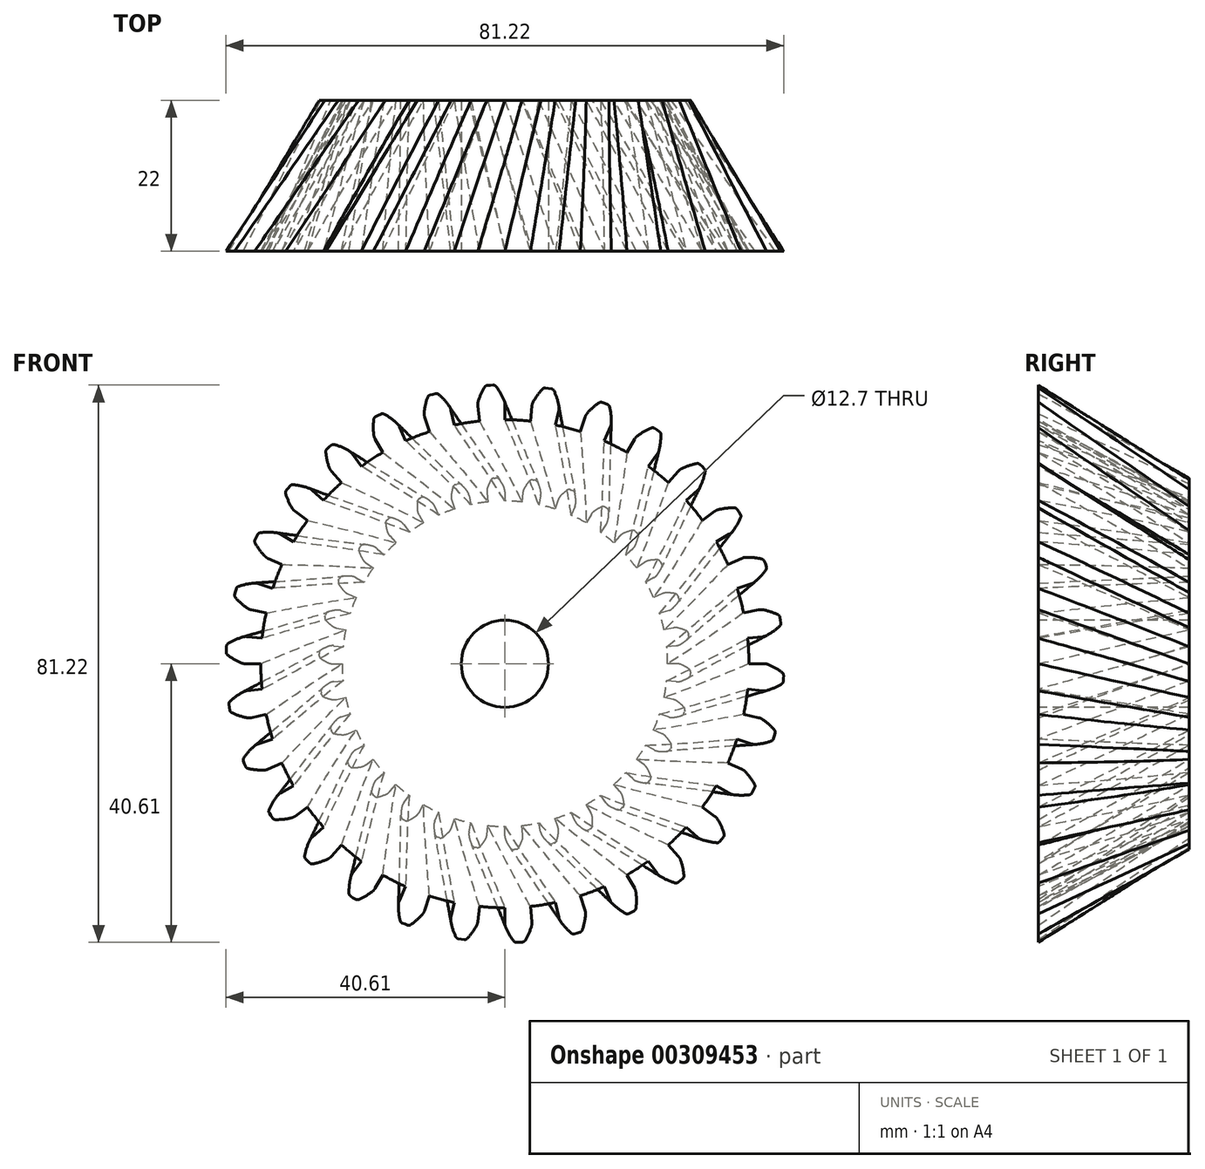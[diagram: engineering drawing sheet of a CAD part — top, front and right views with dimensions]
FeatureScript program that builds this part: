
annotation { "Feature Type Name" : "Feature", "Feature Type Description" : "" }
export const myFeature = defineFeature(function(context is Context, id is Id, definition is map)
    precondition{}
    {
        {
            var Q0;
            Q0=qCreatedBy(makeId("Front.planeOp"),FACE);
            var sketch = newSketch(context, id + "F0", { "sketchPlane" : qUnion([Q0])});
            skCircle(sketch, "E0", {"center": v(0, 0) * mm, "radius": 23.71 * mm});
            skArc(sketch, "E1.trimOffspring", {"start": v(-0.14, 25.74) * mm, "mid": v(-0.44, 26.31) * mm, "end": v(-0.8, 26.85) * mm});
            skLineSegment(sketch, "E2", {"start": v(0, 25.08) * mm, "end": v(0, 23.71) * mm});
            skLineSegment(sketch, "E3", {"start": v(-1.22, 27.06) * mm, "end": v(-1.42, 27.06) * mm});
            skLineSegment(sketch, "E4.MirrorCS", {"start": v(-1.62, 27.04) * mm, "end": v(-1.42, 27.06) * mm});
            skArc(sketch, "E5.MirrorCS", {"start": v(-2.55, 25.61) * mm, "mid": v(-2.31, 26.22) * mm, "end": v(-2.02, 26.79) * mm});
            skLineSegment(sketch, "E6.MirrorCS", {"start": v(-2.62, 24.94) * mm, "end": v(-2.48, 23.58) * mm});
            skPoint(sketch, "E7.visualSharp", {"position": v(-2.66, 25.26) * mm});
            skArc(sketch, "E7.filletArc", {"start": v(-2.55, 25.61) * mm, "mid": v(-2.62, 25.28) * mm, "end": v(-2.62, 24.94) * mm});
            skPoint(sketch, "E8.visualSharp", {"position": v(0, 25.4) * mm});
            skArc(sketch, "E8.filletArc", {"start": v(0, 25.08) * mm, "mid": v(-0.04, 25.42) * mm, "end": v(-0.14, 25.74) * mm});
            skPoint(sketch, "E9.visualSharp", {"position": v(-1.88, 27.02) * mm});
            skArc(sketch, "E9.filletArc", {"start": v(-1.62, 27.04) * mm, "mid": v(-1.85, 26.97) * mm, "end": v(-2.02, 26.79) * mm});
            skPoint(sketch, "E10.visualSharp", {"position": v(-0.96, 27.07) * mm});
            skArc(sketch, "E10.filletArc", {"start": v(-0.8, 26.85) * mm, "mid": v(-0.98, 27.01) * mm, "end": v(-1.22, 27.06) * mm});
            skSolve(sketch);
        }
        {
            var Q0;
            Q0=qCreatedBy(makeId("Front.planeOp"),FACE);
            cPlane(context, id + "F1", {"entities" : qUnion([Q0]), "cplaneType" : CPlaneType.OFFSET, "offset" : 22 * mm, "width" : 152.4 * mm, "height" : 152.4 * mm});
        }
        {
            var Q0;
            Q0=qCreatedBy(id+"F1.planeOp",FACE);
            var sketch = newSketch(context, id + "F2", { "sketchPlane" : qUnion([Q0])});
            skCircle(sketch, "E11", {"center": v(0, 0) * mm, "radius": 35.56 * mm});
            skArc(sketch, "E12.trimOffspring", {"start": v(-0.13, 38.42) * mm, "mid": v(-0.64, 39.44) * mm, "end": v(-1.28, 40.4) * mm});
            skLineSegment(sketch, "E13", {"start": v(0, 37.79) * mm, "end": v(0, 35.56) * mm});
            skLineSegment(sketch, "E14", {"start": v(-1.7, 40.6) * mm, "end": v(-2.13, 40.6) * mm});
            skLineSegment(sketch, "E15.MirrorCS", {"start": v(-2.55, 40.56) * mm, "end": v(-2.13, 40.6) * mm});
            skArc(sketch, "E16.MirrorCS", {"start": v(-3.89, 38.22) * mm, "mid": v(-3.48, 39.3) * mm, "end": v(-2.95, 40.31) * mm});
            skLineSegment(sketch, "E17.MirrorCS", {"start": v(-3.95, 37.58) * mm, "end": v(-3.72, 35.37) * mm});
            skPoint(sketch, "E18.visualSharp", {"position": v(-3.98, 37.9) * mm});
            skArc(sketch, "E18.filletArc", {"start": v(-3.89, 38.22) * mm, "mid": v(-3.95, 37.9) * mm, "end": v(-3.95, 37.58) * mm});
            skPoint(sketch, "E19.visualSharp", {"position": v(0, 38.1) * mm});
            skArc(sketch, "E19.filletArc", {"start": v(0, 37.79) * mm, "mid": v(-0.03, 38.1) * mm, "end": v(-0.13, 38.42) * mm});
            skPoint(sketch, "E20.visualSharp", {"position": v(-2.81, 40.54) * mm});
            skArc(sketch, "E20.filletArc", {"start": v(-2.55, 40.56) * mm, "mid": v(-2.78, 40.49) * mm, "end": v(-2.95, 40.31) * mm});
            skPoint(sketch, "E21.visualSharp", {"position": v(-1.44, 40.61) * mm});
            skArc(sketch, "E21.filletArc", {"start": v(-1.28, 40.4) * mm, "mid": v(-1.46, 40.56) * mm, "end": v(-1.7, 40.6) * mm});
            skLineSegment(sketch, "E22.1.0", {"start": v(-10.93, 39.14) * mm, "end": v(-10.52, 39.26) * mm});
            skLineSegment(sketch, "E22.1.1", {"start": v(-10.1, 39.36) * mm, "end": v(-10.52, 39.26) * mm});
            skArc(sketch, "E22.1.2", {"start": v(-9.65, 39.25) * mm, "mid": v(-9.86, 39.37) * mm, "end": v(-10.1, 39.36) * mm});
            skArc(sketch, "E22.1.3", {"start": v(-10.93, 39.14) * mm, "mid": v(-11.14, 39.02) * mm, "end": v(-11.27, 38.82) * mm});
            skArc(sketch, "E22.1.4", {"start": v(-11.75, 36.58) * mm, "mid": v(-11.58, 37.71) * mm, "end": v(-11.27, 38.82) * mm});
            skArc(sketch, "E22.1.5", {"start": v(-8.11, 37.55) * mm, "mid": v(-8.83, 38.45) * mm, "end": v(-9.65, 39.25) * mm});
            skArc(sketch, "E22.1.6", {"start": v(-7.86, 36.96) * mm, "mid": v(-7.95, 37.27) * mm, "end": v(-8.11, 37.55) * mm});
            skArc(sketch, "E22.1.7", {"start": v(-11.75, 36.58) * mm, "mid": v(-11.75, 36.25) * mm, "end": v(-11.68, 35.94) * mm});
            skLineSegment(sketch, "E22.1.8", {"start": v(-11.68, 35.94) * mm, "end": v(-10.99, 33.82) * mm});
            skLineSegment(sketch, "E22.1.9", {"start": v(-7.86, 36.96) * mm, "end": v(-7.4, 34.78) * mm});
            skLineSegment(sketch, "E22.2.0", {"start": v(-18.83, 36.01) * mm, "end": v(-18.45, 36.22) * mm});
            skLineSegment(sketch, "E22.2.1", {"start": v(-18.07, 36.4) * mm, "end": v(-18.45, 36.22) * mm});
            skArc(sketch, "E22.2.2", {"start": v(-17.6, 36.4) * mm, "mid": v(-17.83, 36.45) * mm, "end": v(-18.07, 36.4) * mm});
            skArc(sketch, "E22.2.3", {"start": v(-18.83, 36.01) * mm, "mid": v(-19.01, 35.85) * mm, "end": v(-19.1, 35.63) * mm});
            skArc(sketch, "E22.2.4", {"start": v(-19.1, 33.33) * mm, "mid": v(-19.17, 34.48) * mm, "end": v(-19.1, 35.63) * mm});
            skArc(sketch, "E22.2.5", {"start": v(-15.74, 35.04) * mm, "mid": v(-16.63, 35.77) * mm, "end": v(-17.6, 36.4) * mm});
            skArc(sketch, "E22.2.6", {"start": v(-15.37, 34.52) * mm, "mid": v(-15.53, 34.8) * mm, "end": v(-15.74, 35.04) * mm});
            skArc(sketch, "E22.2.7", {"start": v(-19.1, 33.33) * mm, "mid": v(-19.03, 33.02) * mm, "end": v(-18.9, 32.73) * mm});
            skLineSegment(sketch, "E22.2.8", {"start": v(-18.9, 32.73) * mm, "end": v(-17.78, 30.8) * mm});
            skLineSegment(sketch, "E22.2.9", {"start": v(-15.37, 34.52) * mm, "end": v(-14.46, 32.49) * mm});
            skLineSegment(sketch, "E22.3.0", {"start": v(-25.9, 31.31) * mm, "end": v(-25.58, 31.59) * mm});
            skLineSegment(sketch, "E22.3.1", {"start": v(-25.24, 31.85) * mm, "end": v(-25.58, 31.59) * mm});
            skArc(sketch, "E22.3.2", {"start": v(-24.78, 31.94) * mm, "mid": v(-25.02, 31.95) * mm, "end": v(-25.24, 31.85) * mm});
            skArc(sketch, "E22.3.3", {"start": v(-25.9, 31.31) * mm, "mid": v(-26.05, 31.12) * mm, "end": v(-26.09, 30.88) * mm});
            skArc(sketch, "E22.3.4", {"start": v(-25.61, 28.63) * mm, "mid": v(-25.92, 29.74) * mm, "end": v(-26.09, 30.88) * mm});
            skArc(sketch, "E22.3.5", {"start": v(-22.68, 31) * mm, "mid": v(-23.7, 31.53) * mm, "end": v(-24.78, 31.94) * mm});
            skArc(sketch, "E22.3.6", {"start": v(-22.21, 30.57) * mm, "mid": v(-22.43, 30.81) * mm, "end": v(-22.68, 31) * mm});
            skArc(sketch, "E22.3.7", {"start": v(-25.61, 28.63) * mm, "mid": v(-25.48, 28.34) * mm, "end": v(-25.29, 28.08) * mm});
            skLineSegment(sketch, "E22.3.8", {"start": v(-25.29, 28.08) * mm, "end": v(-23.8, 26.43) * mm});
            skLineSegment(sketch, "E22.3.9", {"start": v(-22.21, 30.57) * mm, "end": v(-20.9, 28.77) * mm});
            skLineSegment(sketch, "E22.4.0", {"start": v(-31.85, 25.24) * mm, "end": v(-31.59, 25.58) * mm});
            skLineSegment(sketch, "E22.4.1", {"start": v(-31.31, 25.9) * mm, "end": v(-31.59, 25.58) * mm});
            skArc(sketch, "E22.4.2", {"start": v(-30.88, 26.09) * mm, "mid": v(-31.12, 26.05) * mm, "end": v(-31.31, 25.9) * mm});
            skArc(sketch, "E22.4.3", {"start": v(-31.85, 25.24) * mm, "mid": v(-31.95, 25.02) * mm, "end": v(-31.94, 24.78) * mm});
            skArc(sketch, "E22.4.4", {"start": v(-31, 22.68) * mm, "mid": v(-31.53, 23.7) * mm, "end": v(-31.94, 24.78) * mm});
            skArc(sketch, "E22.4.5", {"start": v(-28.63, 25.61) * mm, "mid": v(-29.74, 25.92) * mm, "end": v(-30.88, 26.09) * mm});
            skArc(sketch, "E22.4.6", {"start": v(-28.08, 25.29) * mm, "mid": v(-28.34, 25.48) * mm, "end": v(-28.63, 25.61) * mm});
            skArc(sketch, "E22.4.7", {"start": v(-31, 22.68) * mm, "mid": v(-30.81, 22.43) * mm, "end": v(-30.57, 22.21) * mm});
            skLineSegment(sketch, "E22.4.8", {"start": v(-30.57, 22.21) * mm, "end": v(-28.77, 20.9) * mm});
            skLineSegment(sketch, "E22.4.9", {"start": v(-28.08, 25.29) * mm, "end": v(-26.43, 23.8) * mm});
            skLineSegment(sketch, "E22.5.0", {"start": v(-36.4, 18.07) * mm, "end": v(-36.22, 18.45) * mm});
            skLineSegment(sketch, "E22.5.1", {"start": v(-36.01, 18.83) * mm, "end": v(-36.22, 18.45) * mm});
            skArc(sketch, "E22.5.2", {"start": v(-35.63, 19.1) * mm, "mid": v(-35.85, 19.01) * mm, "end": v(-36.01, 18.83) * mm});
            skArc(sketch, "E22.5.3", {"start": v(-36.4, 18.07) * mm, "mid": v(-36.45, 17.83) * mm, "end": v(-36.4, 17.6) * mm});
            skArc(sketch, "E22.5.4", {"start": v(-35.04, 15.74) * mm, "mid": v(-35.77, 16.63) * mm, "end": v(-36.4, 17.6) * mm});
            skArc(sketch, "E22.5.5", {"start": v(-33.33, 19.1) * mm, "mid": v(-34.48, 19.17) * mm, "end": v(-35.63, 19.1) * mm});
            skArc(sketch, "E22.5.6", {"start": v(-32.73, 18.9) * mm, "mid": v(-33.02, 19.03) * mm, "end": v(-33.33, 19.1) * mm});
            skArc(sketch, "E22.5.7", {"start": v(-35.04, 15.74) * mm, "mid": v(-34.8, 15.53) * mm, "end": v(-34.52, 15.37) * mm});
            skLineSegment(sketch, "E22.5.8", {"start": v(-34.52, 15.37) * mm, "end": v(-32.49, 14.46) * mm});
            skLineSegment(sketch, "E22.5.9", {"start": v(-32.73, 18.9) * mm, "end": v(-30.8, 17.78) * mm});
            skLineSegment(sketch, "E22.6.0", {"start": v(-39.36, 10.1) * mm, "end": v(-39.26, 10.52) * mm});
            skLineSegment(sketch, "E22.6.1", {"start": v(-39.14, 10.93) * mm, "end": v(-39.26, 10.52) * mm});
            skArc(sketch, "E22.6.2", {"start": v(-38.82, 11.27) * mm, "mid": v(-39.02, 11.14) * mm, "end": v(-39.14, 10.93) * mm});
            skArc(sketch, "E22.6.3", {"start": v(-39.36, 10.1) * mm, "mid": v(-39.37, 9.86) * mm, "end": v(-39.25, 9.65) * mm});
            skArc(sketch, "E22.6.4", {"start": v(-37.55, 8.11) * mm, "mid": v(-38.45, 8.83) * mm, "end": v(-39.25, 9.65) * mm});
            skArc(sketch, "E22.6.5", {"start": v(-36.58, 11.75) * mm, "mid": v(-37.71, 11.58) * mm, "end": v(-38.82, 11.27) * mm});
            skArc(sketch, "E22.6.6", {"start": v(-35.94, 11.68) * mm, "mid": v(-36.25, 11.75) * mm, "end": v(-36.58, 11.75) * mm});
            skArc(sketch, "E22.6.7", {"start": v(-37.55, 8.11) * mm, "mid": v(-37.27, 7.95) * mm, "end": v(-36.96, 7.86) * mm});
            skLineSegment(sketch, "E22.6.8", {"start": v(-36.96, 7.86) * mm, "end": v(-34.78, 7.4) * mm});
            skLineSegment(sketch, "E22.6.9", {"start": v(-35.94, 11.68) * mm, "end": v(-33.82, 10.99) * mm});
            skLineSegment(sketch, "E22.7.0", {"start": v(-40.6, 1.7) * mm, "end": v(-40.6, 2.13) * mm});
            skLineSegment(sketch, "E22.7.1", {"start": v(-40.56, 2.55) * mm, "end": v(-40.6, 2.13) * mm});
            skArc(sketch, "E22.7.2", {"start": v(-40.31, 2.95) * mm, "mid": v(-40.49, 2.78) * mm, "end": v(-40.56, 2.55) * mm});
            skArc(sketch, "E22.7.3", {"start": v(-40.6, 1.7) * mm, "mid": v(-40.56, 1.46) * mm, "end": v(-40.4, 1.28) * mm});
            skArc(sketch, "E22.7.4", {"start": v(-38.42, 0.13) * mm, "mid": v(-39.44, 0.64) * mm, "end": v(-40.4, 1.28) * mm});
            skArc(sketch, "E22.7.5", {"start": v(-38.22, 3.89) * mm, "mid": v(-39.3, 3.48) * mm, "end": v(-40.31, 2.95) * mm});
            skArc(sketch, "E22.7.6", {"start": v(-37.58, 3.95) * mm, "mid": v(-37.9, 3.95) * mm, "end": v(-38.22, 3.89) * mm});
            skArc(sketch, "E22.7.7", {"start": v(-38.42, 0.13) * mm, "mid": v(-38.1, 0.03) * mm, "end": v(-37.79, 0) * mm});
            skLineSegment(sketch, "E22.7.8", {"start": v(-37.79, 0) * mm, "end": v(-35.56, 0) * mm});
            skLineSegment(sketch, "E22.7.9", {"start": v(-37.58, 3.95) * mm, "end": v(-35.37, 3.72) * mm});
            skLineSegment(sketch, "E22.8.0", {"start": v(-40.07, -6.78) * mm, "end": v(-40.15, -6.36) * mm});
            skLineSegment(sketch, "E22.8.1", {"start": v(-40.2, -5.93) * mm, "end": v(-40.15, -6.36) * mm});
            skArc(sketch, "E22.8.2", {"start": v(-40.05, -5.5) * mm, "mid": v(-40.18, -5.7) * mm, "end": v(-40.2, -5.93) * mm});
            skArc(sketch, "E22.8.3", {"start": v(-40.07, -6.78) * mm, "mid": v(-39.97, -7) * mm, "end": v(-39.79, -7.15) * mm});
            skArc(sketch, "E22.8.4", {"start": v(-37.6, -7.86) * mm, "mid": v(-38.72, -7.57) * mm, "end": v(-39.79, -7.15) * mm});
            skArc(sketch, "E22.8.5", {"start": v(-38.2, -4.14) * mm, "mid": v(-39.16, -4.76) * mm, "end": v(-40.05, -5.5) * mm});
            skArc(sketch, "E22.8.6", {"start": v(-37.58, -3.95) * mm, "mid": v(-37.9, -4.02) * mm, "end": v(-38.2, -4.14) * mm});
            skArc(sketch, "E22.8.7", {"start": v(-37.6, -7.86) * mm, "mid": v(-37.28, -7.9) * mm, "end": v(-36.96, -7.86) * mm});
            skLineSegment(sketch, "E22.8.8", {"start": v(-36.96, -7.86) * mm, "end": v(-34.78, -7.4) * mm});
            skLineSegment(sketch, "E22.8.9", {"start": v(-37.58, -3.95) * mm, "end": v(-35.37, -3.72) * mm});
            skLineSegment(sketch, "E22.9.0", {"start": v(-37.79, -14.96) * mm, "end": v(-37.95, -14.57) * mm});
            skLineSegment(sketch, "E22.9.1", {"start": v(-38.1, -14.16) * mm, "end": v(-37.95, -14.57) * mm});
            skArc(sketch, "E22.9.2", {"start": v(-38.03, -13.7) * mm, "mid": v(-38.12, -13.92) * mm, "end": v(-38.1, -14.16) * mm});
            skArc(sketch, "E22.9.3", {"start": v(-37.79, -14.96) * mm, "mid": v(-37.64, -15.16) * mm, "end": v(-37.43, -15.27) * mm});
            skArc(sketch, "E22.9.4", {"start": v(-35.15, -15.5) * mm, "mid": v(-36.3, -15.46) * mm, "end": v(-37.43, -15.27) * mm});
            skArc(sketch, "E22.9.5", {"start": v(-36.5, -12) * mm, "mid": v(-37.32, -12.8) * mm, "end": v(-38.03, -13.7) * mm});
            skArc(sketch, "E22.9.6", {"start": v(-35.94, -11.68) * mm, "mid": v(-36.23, -11.8) * mm, "end": v(-36.5, -12) * mm});
            skArc(sketch, "E22.9.7", {"start": v(-35.15, -15.5) * mm, "mid": v(-34.83, -15.47) * mm, "end": v(-34.52, -15.37) * mm});
            skLineSegment(sketch, "E22.9.8", {"start": v(-34.52, -15.37) * mm, "end": v(-32.49, -14.46) * mm});
            skLineSegment(sketch, "E22.9.9", {"start": v(-35.94, -11.68) * mm, "end": v(-33.82, -10.99) * mm});
            skLineSegment(sketch, "E22.10.0", {"start": v(-33.85, -22.5) * mm, "end": v(-34.09, -22.14) * mm});
            skLineSegment(sketch, "E22.10.1", {"start": v(-34.32, -21.77) * mm, "end": v(-34.09, -22.14) * mm});
            skArc(sketch, "E22.10.2", {"start": v(-34.35, -21.3) * mm, "mid": v(-34.4, -21.54) * mm, "end": v(-34.32, -21.77) * mm});
            skArc(sketch, "E22.10.3", {"start": v(-33.85, -22.5) * mm, "mid": v(-33.67, -22.66) * mm, "end": v(-33.44, -22.72) * mm});
            skArc(sketch, "E22.10.4", {"start": v(-31.15, -22.48) * mm, "mid": v(-32.29, -22.67) * mm, "end": v(-33.44, -22.72) * mm});
            skArc(sketch, "E22.10.5", {"start": v(-33.2, -19.32) * mm, "mid": v(-33.84, -20.28) * mm, "end": v(-34.35, -21.3) * mm});
            skArc(sketch, "E22.10.6", {"start": v(-32.73, -18.9) * mm, "mid": v(-32.99, -19.08) * mm, "end": v(-33.2, -19.32) * mm});
            skArc(sketch, "E22.10.7", {"start": v(-31.15, -22.48) * mm, "mid": v(-30.85, -22.37) * mm, "end": v(-30.57, -22.21) * mm});
            skLineSegment(sketch, "E22.10.8", {"start": v(-30.57, -22.21) * mm, "end": v(-28.77, -20.9) * mm});
            skLineSegment(sketch, "E22.10.9", {"start": v(-32.73, -18.9) * mm, "end": v(-30.8, -17.78) * mm});
            skLineSegment(sketch, "E22.11.0", {"start": v(-28.43, -29.04) * mm, "end": v(-28.74, -28.74) * mm});
            skLineSegment(sketch, "E22.11.1", {"start": v(-29.04, -28.43) * mm, "end": v(-28.74, -28.74) * mm});
            skArc(sketch, "E22.11.2", {"start": v(-29.17, -27.98) * mm, "mid": v(-29.16, -28.22) * mm, "end": v(-29.04, -28.43) * mm});
            skArc(sketch, "E22.11.3", {"start": v(-28.43, -29.04) * mm, "mid": v(-28.22, -29.16) * mm, "end": v(-27.98, -29.17) * mm});
            skArc(sketch, "E22.11.4", {"start": v(-25.8, -28.46) * mm, "mid": v(-26.87, -28.88) * mm, "end": v(-27.98, -29.17) * mm});
            skArc(sketch, "E22.11.5", {"start": v(-28.46, -25.8) * mm, "mid": v(-28.88, -26.87) * mm, "end": v(-29.17, -27.98) * mm});
            skArc(sketch, "E22.11.6", {"start": v(-28.08, -25.29) * mm, "mid": v(-28.3, -25.52) * mm, "end": v(-28.46, -25.8) * mm});
            skArc(sketch, "E22.11.7", {"start": v(-25.8, -28.46) * mm, "mid": v(-25.52, -28.3) * mm, "end": v(-25.29, -28.08) * mm});
            skLineSegment(sketch, "E22.11.8", {"start": v(-25.29, -28.08) * mm, "end": v(-23.8, -26.43) * mm});
            skLineSegment(sketch, "E22.11.9", {"start": v(-28.08, -25.29) * mm, "end": v(-26.43, -23.8) * mm});
            skLineSegment(sketch, "E22.12.0", {"start": v(-21.77, -34.32) * mm, "end": v(-22.14, -34.09) * mm});
            skLineSegment(sketch, "E22.12.1", {"start": v(-22.5, -33.85) * mm, "end": v(-22.14, -34.09) * mm});
            skArc(sketch, "E22.12.2", {"start": v(-22.72, -33.44) * mm, "mid": v(-22.66, -33.67) * mm, "end": v(-22.5, -33.85) * mm});
            skArc(sketch, "E22.12.3", {"start": v(-21.77, -34.32) * mm, "mid": v(-21.54, -34.4) * mm, "end": v(-21.3, -34.35) * mm});
            skArc(sketch, "E22.12.4", {"start": v(-19.32, -33.2) * mm, "mid": v(-20.28, -33.84) * mm, "end": v(-21.3, -34.35) * mm});
            skArc(sketch, "E22.12.5", {"start": v(-22.48, -31.15) * mm, "mid": v(-22.67, -32.29) * mm, "end": v(-22.72, -33.44) * mm});
            skArc(sketch, "E22.12.6", {"start": v(-22.21, -30.57) * mm, "mid": v(-22.37, -30.85) * mm, "end": v(-22.48, -31.15) * mm});
            skArc(sketch, "E22.12.7", {"start": v(-19.32, -33.2) * mm, "mid": v(-19.08, -32.99) * mm, "end": v(-18.9, -32.73) * mm});
            skLineSegment(sketch, "E22.12.8", {"start": v(-18.9, -32.73) * mm, "end": v(-17.78, -30.8) * mm});
            skLineSegment(sketch, "E22.12.9", {"start": v(-22.21, -30.57) * mm, "end": v(-20.9, -28.77) * mm});
            skLineSegment(sketch, "E22.13.0", {"start": v(-14.16, -38.1) * mm, "end": v(-14.57, -37.95) * mm});
            skLineSegment(sketch, "E22.13.1", {"start": v(-14.96, -37.79) * mm, "end": v(-14.57, -37.95) * mm});
            skArc(sketch, "E22.13.2", {"start": v(-15.27, -37.43) * mm, "mid": v(-15.16, -37.64) * mm, "end": v(-14.96, -37.79) * mm});
            skArc(sketch, "E22.13.3", {"start": v(-14.16, -38.1) * mm, "mid": v(-13.92, -38.12) * mm, "end": v(-13.7, -38.03) * mm});
            skArc(sketch, "E22.13.4", {"start": v(-12, -36.5) * mm, "mid": v(-12.8, -37.32) * mm, "end": v(-13.7, -38.03) * mm});
            skArc(sketch, "E22.13.5", {"start": v(-15.5, -35.15) * mm, "mid": v(-15.46, -36.3) * mm, "end": v(-15.27, -37.43) * mm});
            skArc(sketch, "E22.13.6", {"start": v(-15.37, -34.52) * mm, "mid": v(-15.47, -34.83) * mm, "end": v(-15.5, -35.15) * mm});
            skArc(sketch, "E22.13.7", {"start": v(-12, -36.5) * mm, "mid": v(-11.8, -36.23) * mm, "end": v(-11.68, -35.94) * mm});
            skLineSegment(sketch, "E22.13.8", {"start": v(-11.68, -35.94) * mm, "end": v(-10.99, -33.82) * mm});
            skLineSegment(sketch, "E22.13.9", {"start": v(-15.37, -34.52) * mm, "end": v(-14.46, -32.49) * mm});
            skLineSegment(sketch, "E22.14.0", {"start": v(-5.93, -40.2) * mm, "end": v(-6.36, -40.15) * mm});
            skLineSegment(sketch, "E22.14.1", {"start": v(-6.78, -40.07) * mm, "end": v(-6.36, -40.15) * mm});
            skArc(sketch, "E22.14.2", {"start": v(-7.15, -39.79) * mm, "mid": v(-7, -39.97) * mm, "end": v(-6.78, -40.07) * mm});
            skArc(sketch, "E22.14.3", {"start": v(-5.93, -40.2) * mm, "mid": v(-5.7, -40.18) * mm, "end": v(-5.5, -40.05) * mm});
            skArc(sketch, "E22.14.4", {"start": v(-4.14, -38.2) * mm, "mid": v(-4.76, -39.16) * mm, "end": v(-5.5, -40.05) * mm});
            skArc(sketch, "E22.14.5", {"start": v(-7.86, -37.6) * mm, "mid": v(-7.57, -38.72) * mm, "end": v(-7.15, -39.79) * mm});
            skArc(sketch, "E22.14.6", {"start": v(-7.86, -36.96) * mm, "mid": v(-7.9, -37.28) * mm, "end": v(-7.86, -37.6) * mm});
            skArc(sketch, "E22.14.7", {"start": v(-4.14, -38.2) * mm, "mid": v(-4.02, -37.9) * mm, "end": v(-3.95, -37.58) * mm});
            skLineSegment(sketch, "E22.14.8", {"start": v(-3.95, -37.58) * mm, "end": v(-3.72, -35.37) * mm});
            skLineSegment(sketch, "E22.14.9", {"start": v(-7.86, -36.96) * mm, "end": v(-7.4, -34.78) * mm});
            skLineSegment(sketch, "E22.15.0", {"start": v(2.55, -40.56) * mm, "end": v(2.13, -40.6) * mm});
            skLineSegment(sketch, "E22.15.1", {"start": v(1.7, -40.6) * mm, "end": v(2.13, -40.6) * mm});
            skArc(sketch, "E22.15.2", {"start": v(1.28, -40.4) * mm, "mid": v(1.46, -40.56) * mm, "end": v(1.7, -40.6) * mm});
            skArc(sketch, "E22.15.3", {"start": v(2.55, -40.56) * mm, "mid": v(2.78, -40.49) * mm, "end": v(2.95, -40.31) * mm});
            skArc(sketch, "E22.15.4", {"start": v(3.89, -38.22) * mm, "mid": v(3.48, -39.3) * mm, "end": v(2.95, -40.31) * mm});
            skArc(sketch, "E22.15.5", {"start": v(0.13, -38.42) * mm, "mid": v(0.64, -39.44) * mm, "end": v(1.28, -40.4) * mm});
            skArc(sketch, "E22.15.6", {"start": v(0, -37.79) * mm, "mid": v(0.03, -38.1) * mm, "end": v(0.13, -38.42) * mm});
            skArc(sketch, "E22.15.7", {"start": v(3.89, -38.22) * mm, "mid": v(3.95, -37.9) * mm, "end": v(3.95, -37.58) * mm});
            skLineSegment(sketch, "E22.15.8", {"start": v(3.95, -37.58) * mm, "end": v(3.72, -35.37) * mm});
            skLineSegment(sketch, "E22.15.9", {"start": v(0, -37.79) * mm, "end": v(0, -35.56) * mm});
            skLineSegment(sketch, "E22.16.0", {"start": v(10.93, -39.14) * mm, "end": v(10.52, -39.26) * mm});
            skLineSegment(sketch, "E22.16.1", {"start": v(10.1, -39.36) * mm, "end": v(10.52, -39.26) * mm});
            skArc(sketch, "E22.16.2", {"start": v(9.65, -39.25) * mm, "mid": v(9.86, -39.37) * mm, "end": v(10.1, -39.36) * mm});
            skArc(sketch, "E22.16.3", {"start": v(10.93, -39.14) * mm, "mid": v(11.14, -39.02) * mm, "end": v(11.27, -38.82) * mm});
            skArc(sketch, "E22.16.4", {"start": v(11.75, -36.58) * mm, "mid": v(11.58, -37.71) * mm, "end": v(11.27, -38.82) * mm});
            skArc(sketch, "E22.16.5", {"start": v(8.11, -37.55) * mm, "mid": v(8.83, -38.45) * mm, "end": v(9.65, -39.25) * mm});
            skArc(sketch, "E22.16.6", {"start": v(7.86, -36.96) * mm, "mid": v(7.95, -37.27) * mm, "end": v(8.11, -37.55) * mm});
            skArc(sketch, "E22.16.7", {"start": v(11.75, -36.58) * mm, "mid": v(11.75, -36.25) * mm, "end": v(11.68, -35.94) * mm});
            skLineSegment(sketch, "E22.16.8", {"start": v(11.68, -35.94) * mm, "end": v(10.99, -33.82) * mm});
            skLineSegment(sketch, "E22.16.9", {"start": v(7.86, -36.96) * mm, "end": v(7.4, -34.78) * mm});
            skLineSegment(sketch, "E22.17.0", {"start": v(18.83, -36.01) * mm, "end": v(18.45, -36.22) * mm});
            skLineSegment(sketch, "E22.17.1", {"start": v(18.07, -36.4) * mm, "end": v(18.45, -36.22) * mm});
            skArc(sketch, "E22.17.2", {"start": v(17.6, -36.4) * mm, "mid": v(17.83, -36.45) * mm, "end": v(18.07, -36.4) * mm});
            skArc(sketch, "E22.17.3", {"start": v(18.83, -36.01) * mm, "mid": v(19.01, -35.85) * mm, "end": v(19.1, -35.63) * mm});
            skArc(sketch, "E22.17.4", {"start": v(19.1, -33.33) * mm, "mid": v(19.17, -34.48) * mm, "end": v(19.1, -35.63) * mm});
            skArc(sketch, "E22.17.5", {"start": v(15.74, -35.04) * mm, "mid": v(16.63, -35.77) * mm, "end": v(17.6, -36.4) * mm});
            skArc(sketch, "E22.17.6", {"start": v(15.37, -34.52) * mm, "mid": v(15.53, -34.8) * mm, "end": v(15.74, -35.04) * mm});
            skArc(sketch, "E22.17.7", {"start": v(19.1, -33.33) * mm, "mid": v(19.03, -33.02) * mm, "end": v(18.9, -32.73) * mm});
            skLineSegment(sketch, "E22.17.8", {"start": v(18.9, -32.73) * mm, "end": v(17.78, -30.8) * mm});
            skLineSegment(sketch, "E22.17.9", {"start": v(15.37, -34.52) * mm, "end": v(14.46, -32.49) * mm});
            skLineSegment(sketch, "E22.18.0", {"start": v(25.9, -31.31) * mm, "end": v(25.58, -31.59) * mm});
            skLineSegment(sketch, "E22.18.1", {"start": v(25.24, -31.85) * mm, "end": v(25.58, -31.59) * mm});
            skArc(sketch, "E22.18.2", {"start": v(24.78, -31.94) * mm, "mid": v(25.02, -31.95) * mm, "end": v(25.24, -31.85) * mm});
            skArc(sketch, "E22.18.3", {"start": v(25.9, -31.31) * mm, "mid": v(26.05, -31.12) * mm, "end": v(26.09, -30.88) * mm});
            skArc(sketch, "E22.18.4", {"start": v(25.61, -28.63) * mm, "mid": v(25.92, -29.74) * mm, "end": v(26.09, -30.88) * mm});
            skArc(sketch, "E22.18.5", {"start": v(22.68, -31) * mm, "mid": v(23.7, -31.53) * mm, "end": v(24.78, -31.94) * mm});
            skArc(sketch, "E22.18.6", {"start": v(22.21, -30.57) * mm, "mid": v(22.43, -30.81) * mm, "end": v(22.68, -31) * mm});
            skArc(sketch, "E22.18.7", {"start": v(25.61, -28.63) * mm, "mid": v(25.48, -28.34) * mm, "end": v(25.29, -28.08) * mm});
            skLineSegment(sketch, "E22.18.8", {"start": v(25.29, -28.08) * mm, "end": v(23.8, -26.43) * mm});
            skLineSegment(sketch, "E22.18.9", {"start": v(22.21, -30.57) * mm, "end": v(20.9, -28.77) * mm});
            skLineSegment(sketch, "E22.19.0", {"start": v(31.85, -25.24) * mm, "end": v(31.59, -25.58) * mm});
            skLineSegment(sketch, "E22.19.1", {"start": v(31.31, -25.9) * mm, "end": v(31.59, -25.58) * mm});
            skArc(sketch, "E22.19.2", {"start": v(30.88, -26.09) * mm, "mid": v(31.12, -26.05) * mm, "end": v(31.31, -25.9) * mm});
            skArc(sketch, "E22.19.3", {"start": v(31.85, -25.24) * mm, "mid": v(31.95, -25.02) * mm, "end": v(31.94, -24.78) * mm});
            skArc(sketch, "E22.19.4", {"start": v(31, -22.68) * mm, "mid": v(31.53, -23.7) * mm, "end": v(31.94, -24.78) * mm});
            skArc(sketch, "E22.19.5", {"start": v(28.63, -25.61) * mm, "mid": v(29.74, -25.92) * mm, "end": v(30.88, -26.09) * mm});
            skArc(sketch, "E22.19.6", {"start": v(28.08, -25.29) * mm, "mid": v(28.34, -25.48) * mm, "end": v(28.63, -25.61) * mm});
            skArc(sketch, "E22.19.7", {"start": v(31, -22.68) * mm, "mid": v(30.81, -22.43) * mm, "end": v(30.57, -22.21) * mm});
            skLineSegment(sketch, "E22.19.8", {"start": v(30.57, -22.21) * mm, "end": v(28.77, -20.9) * mm});
            skLineSegment(sketch, "E22.19.9", {"start": v(28.08, -25.29) * mm, "end": v(26.43, -23.8) * mm});
            skLineSegment(sketch, "E22.20.0", {"start": v(36.4, -18.07) * mm, "end": v(36.22, -18.45) * mm});
            skLineSegment(sketch, "E22.20.1", {"start": v(36.01, -18.83) * mm, "end": v(36.22, -18.45) * mm});
            skArc(sketch, "E22.20.2", {"start": v(35.63, -19.1) * mm, "mid": v(35.85, -19.01) * mm, "end": v(36.01, -18.83) * mm});
            skArc(sketch, "E22.20.3", {"start": v(36.4, -18.07) * mm, "mid": v(36.45, -17.83) * mm, "end": v(36.4, -17.6) * mm});
            skArc(sketch, "E22.20.4", {"start": v(35.04, -15.74) * mm, "mid": v(35.77, -16.63) * mm, "end": v(36.4, -17.6) * mm});
            skArc(sketch, "E22.20.5", {"start": v(33.33, -19.1) * mm, "mid": v(34.48, -19.17) * mm, "end": v(35.63, -19.1) * mm});
            skArc(sketch, "E22.20.6", {"start": v(32.73, -18.9) * mm, "mid": v(33.02, -19.03) * mm, "end": v(33.33, -19.1) * mm});
            skArc(sketch, "E22.20.7", {"start": v(35.04, -15.74) * mm, "mid": v(34.8, -15.53) * mm, "end": v(34.52, -15.37) * mm});
            skLineSegment(sketch, "E22.20.8", {"start": v(34.52, -15.37) * mm, "end": v(32.49, -14.46) * mm});
            skLineSegment(sketch, "E22.20.9", {"start": v(32.73, -18.9) * mm, "end": v(30.8, -17.78) * mm});
            skLineSegment(sketch, "E22.21.0", {"start": v(39.36, -10.1) * mm, "end": v(39.26, -10.52) * mm});
            skLineSegment(sketch, "E22.21.1", {"start": v(39.14, -10.93) * mm, "end": v(39.26, -10.52) * mm});
            skArc(sketch, "E22.21.2", {"start": v(38.82, -11.27) * mm, "mid": v(39.02, -11.14) * mm, "end": v(39.14, -10.93) * mm});
            skArc(sketch, "E22.21.3", {"start": v(39.36, -10.1) * mm, "mid": v(39.37, -9.86) * mm, "end": v(39.25, -9.65) * mm});
            skArc(sketch, "E22.21.4", {"start": v(37.55, -8.11) * mm, "mid": v(38.45, -8.83) * mm, "end": v(39.25, -9.65) * mm});
            skArc(sketch, "E22.21.5", {"start": v(36.58, -11.75) * mm, "mid": v(37.71, -11.58) * mm, "end": v(38.82, -11.27) * mm});
            skArc(sketch, "E22.21.6", {"start": v(35.94, -11.68) * mm, "mid": v(36.25, -11.75) * mm, "end": v(36.58, -11.75) * mm});
            skArc(sketch, "E22.21.7", {"start": v(37.55, -8.11) * mm, "mid": v(37.27, -7.95) * mm, "end": v(36.96, -7.86) * mm});
            skLineSegment(sketch, "E22.21.8", {"start": v(36.96, -7.86) * mm, "end": v(34.78, -7.4) * mm});
            skLineSegment(sketch, "E22.21.9", {"start": v(35.94, -11.68) * mm, "end": v(33.82, -10.99) * mm});
            skLineSegment(sketch, "E22.22.0", {"start": v(40.6, -1.7) * mm, "end": v(40.6, -2.13) * mm});
            skLineSegment(sketch, "E22.22.1", {"start": v(40.56, -2.55) * mm, "end": v(40.6, -2.13) * mm});
            skArc(sketch, "E22.22.2", {"start": v(40.31, -2.95) * mm, "mid": v(40.49, -2.78) * mm, "end": v(40.56, -2.55) * mm});
            skArc(sketch, "E22.22.3", {"start": v(40.6, -1.7) * mm, "mid": v(40.56, -1.46) * mm, "end": v(40.4, -1.28) * mm});
            skArc(sketch, "E22.22.4", {"start": v(38.42, -0.13) * mm, "mid": v(39.44, -0.64) * mm, "end": v(40.4, -1.28) * mm});
            skArc(sketch, "E22.22.5", {"start": v(38.22, -3.89) * mm, "mid": v(39.3, -3.48) * mm, "end": v(40.31, -2.95) * mm});
            skArc(sketch, "E22.22.6", {"start": v(37.58, -3.95) * mm, "mid": v(37.9, -3.95) * mm, "end": v(38.22, -3.89) * mm});
            skArc(sketch, "E22.22.7", {"start": v(38.42, -0.13) * mm, "mid": v(38.1, -0.03) * mm, "end": v(37.79, 0) * mm});
            skLineSegment(sketch, "E22.22.8", {"start": v(37.79, 0) * mm, "end": v(35.56, 0) * mm});
            skLineSegment(sketch, "E22.22.9", {"start": v(37.58, -3.95) * mm, "end": v(35.37, -3.72) * mm});
            skLineSegment(sketch, "E22.23.0", {"start": v(40.07, 6.78) * mm, "end": v(40.15, 6.36) * mm});
            skLineSegment(sketch, "E22.23.1", {"start": v(40.2, 5.93) * mm, "end": v(40.15, 6.36) * mm});
            skArc(sketch, "E22.23.2", {"start": v(40.05, 5.5) * mm, "mid": v(40.18, 5.7) * mm, "end": v(40.2, 5.93) * mm});
            skArc(sketch, "E22.23.3", {"start": v(40.07, 6.78) * mm, "mid": v(39.97, 7) * mm, "end": v(39.79, 7.15) * mm});
            skArc(sketch, "E22.23.4", {"start": v(37.6, 7.86) * mm, "mid": v(38.72, 7.57) * mm, "end": v(39.79, 7.15) * mm});
            skArc(sketch, "E22.23.5", {"start": v(38.2, 4.14) * mm, "mid": v(39.16, 4.76) * mm, "end": v(40.05, 5.5) * mm});
            skArc(sketch, "E22.23.6", {"start": v(37.58, 3.95) * mm, "mid": v(37.9, 4.02) * mm, "end": v(38.2, 4.14) * mm});
            skArc(sketch, "E22.23.7", {"start": v(37.6, 7.86) * mm, "mid": v(37.28, 7.9) * mm, "end": v(36.96, 7.86) * mm});
            skLineSegment(sketch, "E22.23.8", {"start": v(36.96, 7.86) * mm, "end": v(34.78, 7.4) * mm});
            skLineSegment(sketch, "E22.23.9", {"start": v(37.58, 3.95) * mm, "end": v(35.37, 3.72) * mm});
            skLineSegment(sketch, "E22.24.0", {"start": v(37.79, 14.96) * mm, "end": v(37.95, 14.57) * mm});
            skLineSegment(sketch, "E22.24.1", {"start": v(38.1, 14.16) * mm, "end": v(37.95, 14.57) * mm});
            skArc(sketch, "E22.24.2", {"start": v(38.03, 13.7) * mm, "mid": v(38.12, 13.92) * mm, "end": v(38.1, 14.16) * mm});
            skArc(sketch, "E22.24.3", {"start": v(37.79, 14.96) * mm, "mid": v(37.64, 15.16) * mm, "end": v(37.43, 15.27) * mm});
            skArc(sketch, "E22.24.4", {"start": v(35.15, 15.5) * mm, "mid": v(36.3, 15.46) * mm, "end": v(37.43, 15.27) * mm});
            skArc(sketch, "E22.24.5", {"start": v(36.5, 12) * mm, "mid": v(37.32, 12.8) * mm, "end": v(38.03, 13.7) * mm});
            skArc(sketch, "E22.24.6", {"start": v(35.94, 11.68) * mm, "mid": v(36.23, 11.8) * mm, "end": v(36.5, 12) * mm});
            skArc(sketch, "E22.24.7", {"start": v(35.15, 15.5) * mm, "mid": v(34.83, 15.47) * mm, "end": v(34.52, 15.37) * mm});
            skLineSegment(sketch, "E22.24.8", {"start": v(34.52, 15.37) * mm, "end": v(32.49, 14.46) * mm});
            skLineSegment(sketch, "E22.24.9", {"start": v(35.94, 11.68) * mm, "end": v(33.82, 10.99) * mm});
            skLineSegment(sketch, "E22.25.0", {"start": v(33.85, 22.5) * mm, "end": v(34.09, 22.14) * mm});
            skLineSegment(sketch, "E22.25.1", {"start": v(34.32, 21.77) * mm, "end": v(34.09, 22.14) * mm});
            skArc(sketch, "E22.25.2", {"start": v(34.35, 21.3) * mm, "mid": v(34.4, 21.54) * mm, "end": v(34.32, 21.77) * mm});
            skArc(sketch, "E22.25.3", {"start": v(33.85, 22.5) * mm, "mid": v(33.67, 22.66) * mm, "end": v(33.44, 22.72) * mm});
            skArc(sketch, "E22.25.4", {"start": v(31.15, 22.48) * mm, "mid": v(32.29, 22.67) * mm, "end": v(33.44, 22.72) * mm});
            skArc(sketch, "E22.25.5", {"start": v(33.2, 19.32) * mm, "mid": v(33.84, 20.28) * mm, "end": v(34.35, 21.3) * mm});
            skArc(sketch, "E22.25.6", {"start": v(32.73, 18.9) * mm, "mid": v(32.99, 19.08) * mm, "end": v(33.2, 19.32) * mm});
            skArc(sketch, "E22.25.7", {"start": v(31.15, 22.48) * mm, "mid": v(30.85, 22.37) * mm, "end": v(30.57, 22.21) * mm});
            skLineSegment(sketch, "E22.25.8", {"start": v(30.57, 22.21) * mm, "end": v(28.77, 20.9) * mm});
            skLineSegment(sketch, "E22.25.9", {"start": v(32.73, 18.9) * mm, "end": v(30.8, 17.78) * mm});
            skLineSegment(sketch, "E22.26.0", {"start": v(28.43, 29.04) * mm, "end": v(28.74, 28.74) * mm});
            skLineSegment(sketch, "E22.26.1", {"start": v(29.04, 28.43) * mm, "end": v(28.74, 28.74) * mm});
            skArc(sketch, "E22.26.2", {"start": v(29.17, 27.98) * mm, "mid": v(29.16, 28.22) * mm, "end": v(29.04, 28.43) * mm});
            skArc(sketch, "E22.26.3", {"start": v(28.43, 29.04) * mm, "mid": v(28.22, 29.16) * mm, "end": v(27.98, 29.17) * mm});
            skArc(sketch, "E22.26.4", {"start": v(25.8, 28.46) * mm, "mid": v(26.87, 28.88) * mm, "end": v(27.98, 29.17) * mm});
            skArc(sketch, "E22.26.5", {"start": v(28.46, 25.8) * mm, "mid": v(28.88, 26.87) * mm, "end": v(29.17, 27.98) * mm});
            skArc(sketch, "E22.26.6", {"start": v(28.08, 25.29) * mm, "mid": v(28.3, 25.52) * mm, "end": v(28.46, 25.8) * mm});
            skArc(sketch, "E22.26.7", {"start": v(25.8, 28.46) * mm, "mid": v(25.52, 28.3) * mm, "end": v(25.29, 28.08) * mm});
            skLineSegment(sketch, "E22.26.8", {"start": v(25.29, 28.08) * mm, "end": v(23.8, 26.43) * mm});
            skLineSegment(sketch, "E22.26.9", {"start": v(28.08, 25.29) * mm, "end": v(26.43, 23.8) * mm});
            skLineSegment(sketch, "E22.27.0", {"start": v(21.77, 34.32) * mm, "end": v(22.14, 34.09) * mm});
            skLineSegment(sketch, "E22.27.1", {"start": v(22.5, 33.85) * mm, "end": v(22.14, 34.09) * mm});
            skArc(sketch, "E22.27.2", {"start": v(22.72, 33.44) * mm, "mid": v(22.66, 33.67) * mm, "end": v(22.5, 33.85) * mm});
            skArc(sketch, "E22.27.3", {"start": v(21.77, 34.32) * mm, "mid": v(21.54, 34.4) * mm, "end": v(21.3, 34.35) * mm});
            skArc(sketch, "E22.27.4", {"start": v(19.32, 33.2) * mm, "mid": v(20.28, 33.84) * mm, "end": v(21.3, 34.35) * mm});
            skArc(sketch, "E22.27.5", {"start": v(22.48, 31.15) * mm, "mid": v(22.67, 32.29) * mm, "end": v(22.72, 33.44) * mm});
            skArc(sketch, "E22.27.6", {"start": v(22.21, 30.57) * mm, "mid": v(22.37, 30.85) * mm, "end": v(22.48, 31.15) * mm});
            skArc(sketch, "E22.27.7", {"start": v(19.32, 33.2) * mm, "mid": v(19.08, 32.99) * mm, "end": v(18.9, 32.73) * mm});
            skLineSegment(sketch, "E22.27.8", {"start": v(18.9, 32.73) * mm, "end": v(17.78, 30.8) * mm});
            skLineSegment(sketch, "E22.27.9", {"start": v(22.21, 30.57) * mm, "end": v(20.9, 28.77) * mm});
            skLineSegment(sketch, "E22.28.0", {"start": v(14.16, 38.1) * mm, "end": v(14.57, 37.95) * mm});
            skLineSegment(sketch, "E22.28.1", {"start": v(14.96, 37.79) * mm, "end": v(14.57, 37.95) * mm});
            skArc(sketch, "E22.28.2", {"start": v(15.27, 37.43) * mm, "mid": v(15.16, 37.64) * mm, "end": v(14.96, 37.79) * mm});
            skArc(sketch, "E22.28.3", {"start": v(14.16, 38.1) * mm, "mid": v(13.92, 38.12) * mm, "end": v(13.7, 38.03) * mm});
            skArc(sketch, "E22.28.4", {"start": v(12, 36.5) * mm, "mid": v(12.8, 37.32) * mm, "end": v(13.7, 38.03) * mm});
            skArc(sketch, "E22.28.5", {"start": v(15.5, 35.15) * mm, "mid": v(15.46, 36.3) * mm, "end": v(15.27, 37.43) * mm});
            skArc(sketch, "E22.28.6", {"start": v(15.37, 34.52) * mm, "mid": v(15.47, 34.83) * mm, "end": v(15.5, 35.15) * mm});
            skArc(sketch, "E22.28.7", {"start": v(12, 36.5) * mm, "mid": v(11.8, 36.23) * mm, "end": v(11.68, 35.94) * mm});
            skLineSegment(sketch, "E22.28.8", {"start": v(11.68, 35.94) * mm, "end": v(10.99, 33.82) * mm});
            skLineSegment(sketch, "E22.28.9", {"start": v(15.37, 34.52) * mm, "end": v(14.46, 32.49) * mm});
            skLineSegment(sketch, "E22.29.0", {"start": v(5.93, 40.2) * mm, "end": v(6.36, 40.15) * mm});
            skLineSegment(sketch, "E22.29.1", {"start": v(6.78, 40.07) * mm, "end": v(6.36, 40.15) * mm});
            skArc(sketch, "E22.29.2", {"start": v(7.15, 39.79) * mm, "mid": v(7, 39.97) * mm, "end": v(6.78, 40.07) * mm});
            skArc(sketch, "E22.29.3", {"start": v(5.93, 40.2) * mm, "mid": v(5.7, 40.18) * mm, "end": v(5.5, 40.05) * mm});
            skArc(sketch, "E22.29.4", {"start": v(4.14, 38.2) * mm, "mid": v(4.76, 39.16) * mm, "end": v(5.5, 40.05) * mm});
            skArc(sketch, "E22.29.5", {"start": v(7.86, 37.6) * mm, "mid": v(7.57, 38.72) * mm, "end": v(7.15, 39.79) * mm});
            skArc(sketch, "E22.29.6", {"start": v(7.86, 36.96) * mm, "mid": v(7.9, 37.28) * mm, "end": v(7.86, 37.6) * mm});
            skArc(sketch, "E22.29.7", {"start": v(4.14, 38.2) * mm, "mid": v(4.02, 37.9) * mm, "end": v(3.95, 37.58) * mm});
            skLineSegment(sketch, "E22.29.8", {"start": v(3.95, 37.58) * mm, "end": v(3.72, 35.37) * mm});
            skLineSegment(sketch, "E22.29.9", {"start": v(7.86, 36.96) * mm, "end": v(7.4, 34.78) * mm});
            skSolve(sketch);
        }
        {
            var Q0;
            Q0=makeQuery(id+"F0.imprint","IMPRINT",FACE,{"disambiguationData":[TD([[makeQuery(id+"F0.imprint","IMPRINT",EDGE,{"derivedFrom":sQuery(id+"F0.wireOp",EDGE,"E1.trimOffspring")}),1.0]])]});
            var Q1;
            Q1=makeQuery(id+"F2.imprint","IMPRINT",FACE,{"disambiguationData":[TD([[makeQuery(id+"F2.imprint","IMPRINT",EDGE,{"derivedFrom":sQuery(id+"F2.wireOp",EDGE,"E22.1.0")}),-1.0]])]});
            loft(context, id + "F3", {"sheetProfilesArray" : [{ "sheetProfileEntities" : qUnion([Q0]) }, { "sheetProfileEntities" : qUnion([Q1]) }]});
        }
        {
            var Q0;
            Q0=qCreatedBy(makeId("Front.planeOp"),FACE);
            var sketch = newSketch(context, id + "F4", { "sketchPlane" : qUnion([Q0])});
            skCircle(sketch, "E23", {"center": v(0, 0) * mm, "radius": 23.71 * mm});
            skSolve(sketch);
        }
        {
            var Q0;
            Q0=qCreatedBy(id+"F1.planeOp",FACE);
            var sketch = newSketch(context, id + "F5", { "sketchPlane" : qUnion([Q0])});
            skCircle(sketch, "E24", {"center": v(0, 0) * mm, "radius": 35.56 * mm});
            skSolve(sketch);
        }
        {
            var Q1;
            Q1=makeQuery(id+"F4.imprint","IMPRINT",FACE,{"disambiguationData":[TD([[makeQuery(id+"F4.imprint","IMPRINT",EDGE,{"derivedFrom":sQuery(id+"F4.wireOp",EDGE,"E23")}),1.0]])]});
            var Q2;
            Q2=makeQuery(id+"F5.imprint","IMPRINT",FACE,{"disambiguationData":[TD([[makeQuery(id+"F5.imprint","IMPRINT",EDGE,{"derivedFrom":sQuery(id+"F5.wireOp",EDGE,"E24")}),1.0]])]});
            loft(context, id + "F6", {"operationType" : NewBodyOperationType.ADD, "sheetProfilesArray" : [{ "sheetProfileEntities" : qUnion([Q1]) }, { "sheetProfileEntities" : qUnion([Q2]) }]});
        }
        {
            var Q0;
            Q0=makeQuery(id+"F3.opLoft","SWEPT_BODY",BODY,{"disambiguationData":[OSD([makeQuery(id+"F0.imprint","IMPRINT",FACE,{"disambiguationData":[TD([[makeQuery(id+"F0.imprint","IMPRINT",EDGE,{"derivedFrom":sQuery(id+"F0.wireOp",EDGE,"E1.trimOffspring")}),1.0]])]}),makeQuery(id+"F2.imprint","IMPRINT",FACE,{"disambiguationData":[TD([[makeQuery(id+"F2.imprint","IMPRINT",EDGE,{"derivedFrom":sQuery(id+"F2.wireOp",EDGE,"E22.1.0")}),-1.0]])]})])]});
            var Q1;
            Q1=makeQuery(id+"F6.opLoft","SWEPT_FACE",FACE,{"disambiguationData":[OSD([sQuery(id+"F4.wireOp",EDGE,"E23"),sQuery(id+"F5.wireOp",EDGE,"E24")])]});
            circularPattern(context, id + "F7", {"entities" : qUnion([Q0]), "axis" : qUnion([Q1]), "angle" : 360 * degree, "instanceCount" : 30, "equalSpace" : true});
        }
        {
            var Q0;
            Q0=makeQuery(id+"F7.opPattern","COPY",BODY,{"derivedFrom":makeQuery(id+"F3.opLoft","SWEPT_BODY",BODY,{"disambiguationData":[OSD([makeQuery(id+"F0.imprint","IMPRINT",FACE,{"disambiguationData":[TD([[makeQuery(id+"F0.imprint","IMPRINT",EDGE,{"derivedFrom":sQuery(id+"F0.wireOp",EDGE,"E1.trimOffspring")}),1.0]])]}),makeQuery(id+"F2.imprint","IMPRINT",FACE,{"disambiguationData":[TD([[makeQuery(id+"F2.imprint","IMPRINT",EDGE,{"derivedFrom":sQuery(id+"F2.wireOp",EDGE,"E22.1.0")}),-1.0]])]})])]}),"instanceName":"1"});
            var Q1;
            Q1=makeQuery(id+"F7.opPattern","COPY",BODY,{"derivedFrom":makeQuery(id+"F3.opLoft","SWEPT_BODY",BODY,{"disambiguationData":[OSD([makeQuery(id+"F0.imprint","IMPRINT",FACE,{"disambiguationData":[TD([[makeQuery(id+"F0.imprint","IMPRINT",EDGE,{"derivedFrom":sQuery(id+"F0.wireOp",EDGE,"E1.trimOffspring")}),1.0]])]}),makeQuery(id+"F2.imprint","IMPRINT",FACE,{"disambiguationData":[TD([[makeQuery(id+"F2.imprint","IMPRINT",EDGE,{"derivedFrom":sQuery(id+"F2.wireOp",EDGE,"E22.1.0")}),-1.0]])]})])]}),"instanceName":"29"});
            var Q2;
            Q2=makeQuery(id+"F3.opLoft","SWEPT_BODY",BODY,{"disambiguationData":[OSD([makeQuery(id+"F0.imprint","IMPRINT",FACE,{"disambiguationData":[TD([[makeQuery(id+"F0.imprint","IMPRINT",EDGE,{"derivedFrom":sQuery(id+"F0.wireOp",EDGE,"E1.trimOffspring")}),1.0]])]}),makeQuery(id+"F2.imprint","IMPRINT",FACE,{"disambiguationData":[TD([[makeQuery(id+"F2.imprint","IMPRINT",EDGE,{"derivedFrom":sQuery(id+"F2.wireOp",EDGE,"E22.1.0")}),-1.0]])]})])]});
            var Q3;
            Q3=makeQuery(id+"F7.opPattern","COPY",BODY,{"derivedFrom":makeQuery(id+"F3.opLoft","SWEPT_BODY",BODY,{"disambiguationData":[OSD([makeQuery(id+"F0.imprint","IMPRINT",FACE,{"disambiguationData":[TD([[makeQuery(id+"F0.imprint","IMPRINT",EDGE,{"derivedFrom":sQuery(id+"F0.wireOp",EDGE,"E1.trimOffspring")}),1.0]])]}),makeQuery(id+"F2.imprint","IMPRINT",FACE,{"disambiguationData":[TD([[makeQuery(id+"F2.imprint","IMPRINT",EDGE,{"derivedFrom":sQuery(id+"F2.wireOp",EDGE,"E22.1.0")}),-1.0]])]})])]}),"instanceName":"28"});
            var Q4;
            Q4=makeQuery(id+"F7.opPattern","COPY",BODY,{"derivedFrom":makeQuery(id+"F3.opLoft","SWEPT_BODY",BODY,{"disambiguationData":[OSD([makeQuery(id+"F0.imprint","IMPRINT",FACE,{"disambiguationData":[TD([[makeQuery(id+"F0.imprint","IMPRINT",EDGE,{"derivedFrom":sQuery(id+"F0.wireOp",EDGE,"E1.trimOffspring")}),1.0]])]}),makeQuery(id+"F2.imprint","IMPRINT",FACE,{"disambiguationData":[TD([[makeQuery(id+"F2.imprint","IMPRINT",EDGE,{"derivedFrom":sQuery(id+"F2.wireOp",EDGE,"E22.1.0")}),-1.0]])]})])]}),"instanceName":"27"});
            var Q5;
            Q5=makeQuery(id+"F7.opPattern","COPY",BODY,{"derivedFrom":makeQuery(id+"F3.opLoft","SWEPT_BODY",BODY,{"disambiguationData":[OSD([makeQuery(id+"F0.imprint","IMPRINT",FACE,{"disambiguationData":[TD([[makeQuery(id+"F0.imprint","IMPRINT",EDGE,{"derivedFrom":sQuery(id+"F0.wireOp",EDGE,"E1.trimOffspring")}),1.0]])]}),makeQuery(id+"F2.imprint","IMPRINT",FACE,{"disambiguationData":[TD([[makeQuery(id+"F2.imprint","IMPRINT",EDGE,{"derivedFrom":sQuery(id+"F2.wireOp",EDGE,"E22.1.0")}),-1.0]])]})])]}),"instanceName":"26"});
            var Q6;
            Q6=makeQuery(id+"F7.opPattern","COPY",BODY,{"derivedFrom":makeQuery(id+"F3.opLoft","SWEPT_BODY",BODY,{"disambiguationData":[OSD([makeQuery(id+"F0.imprint","IMPRINT",FACE,{"disambiguationData":[TD([[makeQuery(id+"F0.imprint","IMPRINT",EDGE,{"derivedFrom":sQuery(id+"F0.wireOp",EDGE,"E1.trimOffspring")}),1.0]])]}),makeQuery(id+"F2.imprint","IMPRINT",FACE,{"disambiguationData":[TD([[makeQuery(id+"F2.imprint","IMPRINT",EDGE,{"derivedFrom":sQuery(id+"F2.wireOp",EDGE,"E22.1.0")}),-1.0]])]})])]}),"instanceName":"25"});
            var Q7;
            Q7=makeQuery(id+"F7.opPattern","COPY",BODY,{"derivedFrom":makeQuery(id+"F3.opLoft","SWEPT_BODY",BODY,{"disambiguationData":[OSD([makeQuery(id+"F0.imprint","IMPRINT",FACE,{"disambiguationData":[TD([[makeQuery(id+"F0.imprint","IMPRINT",EDGE,{"derivedFrom":sQuery(id+"F0.wireOp",EDGE,"E1.trimOffspring")}),1.0]])]}),makeQuery(id+"F2.imprint","IMPRINT",FACE,{"disambiguationData":[TD([[makeQuery(id+"F2.imprint","IMPRINT",EDGE,{"derivedFrom":sQuery(id+"F2.wireOp",EDGE,"E22.1.0")}),-1.0]])]})])]}),"instanceName":"24"});
            var Q8;
            Q8=makeQuery(id+"F7.opPattern","COPY",BODY,{"derivedFrom":makeQuery(id+"F3.opLoft","SWEPT_BODY",BODY,{"disambiguationData":[OSD([makeQuery(id+"F0.imprint","IMPRINT",FACE,{"disambiguationData":[TD([[makeQuery(id+"F0.imprint","IMPRINT",EDGE,{"derivedFrom":sQuery(id+"F0.wireOp",EDGE,"E1.trimOffspring")}),1.0]])]}),makeQuery(id+"F2.imprint","IMPRINT",FACE,{"disambiguationData":[TD([[makeQuery(id+"F2.imprint","IMPRINT",EDGE,{"derivedFrom":sQuery(id+"F2.wireOp",EDGE,"E22.1.0")}),-1.0]])]})])]}),"instanceName":"23"});
            var Q9;
            Q9=makeQuery(id+"F7.opPattern","COPY",BODY,{"derivedFrom":makeQuery(id+"F3.opLoft","SWEPT_BODY",BODY,{"disambiguationData":[OSD([makeQuery(id+"F0.imprint","IMPRINT",FACE,{"disambiguationData":[TD([[makeQuery(id+"F0.imprint","IMPRINT",EDGE,{"derivedFrom":sQuery(id+"F0.wireOp",EDGE,"E1.trimOffspring")}),1.0]])]}),makeQuery(id+"F2.imprint","IMPRINT",FACE,{"disambiguationData":[TD([[makeQuery(id+"F2.imprint","IMPRINT",EDGE,{"derivedFrom":sQuery(id+"F2.wireOp",EDGE,"E22.1.0")}),-1.0]])]})])]}),"instanceName":"22"});
            var Q10;
            Q10=makeQuery(id+"F7.opPattern","COPY",BODY,{"derivedFrom":makeQuery(id+"F3.opLoft","SWEPT_BODY",BODY,{"disambiguationData":[OSD([makeQuery(id+"F0.imprint","IMPRINT",FACE,{"disambiguationData":[TD([[makeQuery(id+"F0.imprint","IMPRINT",EDGE,{"derivedFrom":sQuery(id+"F0.wireOp",EDGE,"E1.trimOffspring")}),1.0]])]}),makeQuery(id+"F2.imprint","IMPRINT",FACE,{"disambiguationData":[TD([[makeQuery(id+"F2.imprint","IMPRINT",EDGE,{"derivedFrom":sQuery(id+"F2.wireOp",EDGE,"E22.1.0")}),-1.0]])]})])]}),"instanceName":"21"});
            var Q11;
            Q11=makeQuery(id+"F7.opPattern","COPY",BODY,{"derivedFrom":makeQuery(id+"F3.opLoft","SWEPT_BODY",BODY,{"disambiguationData":[OSD([makeQuery(id+"F0.imprint","IMPRINT",FACE,{"disambiguationData":[TD([[makeQuery(id+"F0.imprint","IMPRINT",EDGE,{"derivedFrom":sQuery(id+"F0.wireOp",EDGE,"E1.trimOffspring")}),1.0]])]}),makeQuery(id+"F2.imprint","IMPRINT",FACE,{"disambiguationData":[TD([[makeQuery(id+"F2.imprint","IMPRINT",EDGE,{"derivedFrom":sQuery(id+"F2.wireOp",EDGE,"E22.1.0")}),-1.0]])]})])]}),"instanceName":"4"});
            var Q12;
            Q12=makeQuery(id+"F7.opPattern","COPY",BODY,{"derivedFrom":makeQuery(id+"F3.opLoft","SWEPT_BODY",BODY,{"disambiguationData":[OSD([makeQuery(id+"F0.imprint","IMPRINT",FACE,{"disambiguationData":[TD([[makeQuery(id+"F0.imprint","IMPRINT",EDGE,{"derivedFrom":sQuery(id+"F0.wireOp",EDGE,"E1.trimOffspring")}),1.0]])]}),makeQuery(id+"F2.imprint","IMPRINT",FACE,{"disambiguationData":[TD([[makeQuery(id+"F2.imprint","IMPRINT",EDGE,{"derivedFrom":sQuery(id+"F2.wireOp",EDGE,"E22.1.0")}),-1.0]])]})])]}),"instanceName":"19"});
            var Q13;
            Q13=makeQuery(id+"F7.opPattern","COPY",BODY,{"derivedFrom":makeQuery(id+"F3.opLoft","SWEPT_BODY",BODY,{"disambiguationData":[OSD([makeQuery(id+"F0.imprint","IMPRINT",FACE,{"disambiguationData":[TD([[makeQuery(id+"F0.imprint","IMPRINT",EDGE,{"derivedFrom":sQuery(id+"F0.wireOp",EDGE,"E1.trimOffspring")}),1.0]])]}),makeQuery(id+"F2.imprint","IMPRINT",FACE,{"disambiguationData":[TD([[makeQuery(id+"F2.imprint","IMPRINT",EDGE,{"derivedFrom":sQuery(id+"F2.wireOp",EDGE,"E22.1.0")}),-1.0]])]})])]}),"instanceName":"18"});
            var Q14;
            Q14=makeQuery(id+"F7.opPattern","COPY",BODY,{"derivedFrom":makeQuery(id+"F3.opLoft","SWEPT_BODY",BODY,{"disambiguationData":[OSD([makeQuery(id+"F0.imprint","IMPRINT",FACE,{"disambiguationData":[TD([[makeQuery(id+"F0.imprint","IMPRINT",EDGE,{"derivedFrom":sQuery(id+"F0.wireOp",EDGE,"E1.trimOffspring")}),1.0]])]}),makeQuery(id+"F2.imprint","IMPRINT",FACE,{"disambiguationData":[TD([[makeQuery(id+"F2.imprint","IMPRINT",EDGE,{"derivedFrom":sQuery(id+"F2.wireOp",EDGE,"E22.1.0")}),-1.0]])]})])]}),"instanceName":"16"});
            var Q15;
            Q15=makeQuery(id+"F7.opPattern","COPY",BODY,{"derivedFrom":makeQuery(id+"F3.opLoft","SWEPT_BODY",BODY,{"disambiguationData":[OSD([makeQuery(id+"F0.imprint","IMPRINT",FACE,{"disambiguationData":[TD([[makeQuery(id+"F0.imprint","IMPRINT",EDGE,{"derivedFrom":sQuery(id+"F0.wireOp",EDGE,"E1.trimOffspring")}),1.0]])]}),makeQuery(id+"F2.imprint","IMPRINT",FACE,{"disambiguationData":[TD([[makeQuery(id+"F2.imprint","IMPRINT",EDGE,{"derivedFrom":sQuery(id+"F2.wireOp",EDGE,"E22.1.0")}),-1.0]])]})])]}),"instanceName":"15"});
            var Q16;
            Q16=makeQuery(id+"F7.opPattern","COPY",BODY,{"derivedFrom":makeQuery(id+"F3.opLoft","SWEPT_BODY",BODY,{"disambiguationData":[OSD([makeQuery(id+"F0.imprint","IMPRINT",FACE,{"disambiguationData":[TD([[makeQuery(id+"F0.imprint","IMPRINT",EDGE,{"derivedFrom":sQuery(id+"F0.wireOp",EDGE,"E1.trimOffspring")}),1.0]])]}),makeQuery(id+"F2.imprint","IMPRINT",FACE,{"disambiguationData":[TD([[makeQuery(id+"F2.imprint","IMPRINT",EDGE,{"derivedFrom":sQuery(id+"F2.wireOp",EDGE,"E22.1.0")}),-1.0]])]})])]}),"instanceName":"14"});
            var Q17;
            Q17=makeQuery(id+"F7.opPattern","COPY",BODY,{"derivedFrom":makeQuery(id+"F3.opLoft","SWEPT_BODY",BODY,{"disambiguationData":[OSD([makeQuery(id+"F0.imprint","IMPRINT",FACE,{"disambiguationData":[TD([[makeQuery(id+"F0.imprint","IMPRINT",EDGE,{"derivedFrom":sQuery(id+"F0.wireOp",EDGE,"E1.trimOffspring")}),1.0]])]}),makeQuery(id+"F2.imprint","IMPRINT",FACE,{"disambiguationData":[TD([[makeQuery(id+"F2.imprint","IMPRINT",EDGE,{"derivedFrom":sQuery(id+"F2.wireOp",EDGE,"E22.1.0")}),-1.0]])]})])]}),"instanceName":"13"});
            var Q18;
            Q18=makeQuery(id+"F7.opPattern","COPY",BODY,{"derivedFrom":makeQuery(id+"F3.opLoft","SWEPT_BODY",BODY,{"disambiguationData":[OSD([makeQuery(id+"F0.imprint","IMPRINT",FACE,{"disambiguationData":[TD([[makeQuery(id+"F0.imprint","IMPRINT",EDGE,{"derivedFrom":sQuery(id+"F0.wireOp",EDGE,"E1.trimOffspring")}),1.0]])]}),makeQuery(id+"F2.imprint","IMPRINT",FACE,{"disambiguationData":[TD([[makeQuery(id+"F2.imprint","IMPRINT",EDGE,{"derivedFrom":sQuery(id+"F2.wireOp",EDGE,"E22.1.0")}),-1.0]])]})])]}),"instanceName":"12"});
            var Q19;
            Q19=makeQuery(id+"F7.opPattern","COPY",BODY,{"derivedFrom":makeQuery(id+"F3.opLoft","SWEPT_BODY",BODY,{"disambiguationData":[OSD([makeQuery(id+"F0.imprint","IMPRINT",FACE,{"disambiguationData":[TD([[makeQuery(id+"F0.imprint","IMPRINT",EDGE,{"derivedFrom":sQuery(id+"F0.wireOp",EDGE,"E1.trimOffspring")}),1.0]])]}),makeQuery(id+"F2.imprint","IMPRINT",FACE,{"disambiguationData":[TD([[makeQuery(id+"F2.imprint","IMPRINT",EDGE,{"derivedFrom":sQuery(id+"F2.wireOp",EDGE,"E22.1.0")}),-1.0]])]})])]}),"instanceName":"11"});
            var Q20;
            Q20=makeQuery(id+"F7.opPattern","COPY",BODY,{"derivedFrom":makeQuery(id+"F3.opLoft","SWEPT_BODY",BODY,{"disambiguationData":[OSD([makeQuery(id+"F0.imprint","IMPRINT",FACE,{"disambiguationData":[TD([[makeQuery(id+"F0.imprint","IMPRINT",EDGE,{"derivedFrom":sQuery(id+"F0.wireOp",EDGE,"E1.trimOffspring")}),1.0]])]}),makeQuery(id+"F2.imprint","IMPRINT",FACE,{"disambiguationData":[TD([[makeQuery(id+"F2.imprint","IMPRINT",EDGE,{"derivedFrom":sQuery(id+"F2.wireOp",EDGE,"E22.1.0")}),-1.0]])]})])]}),"instanceName":"10"});
            var Q21;
            Q21=makeQuery(id+"F7.opPattern","COPY",BODY,{"derivedFrom":makeQuery(id+"F3.opLoft","SWEPT_BODY",BODY,{"disambiguationData":[OSD([makeQuery(id+"F0.imprint","IMPRINT",FACE,{"disambiguationData":[TD([[makeQuery(id+"F0.imprint","IMPRINT",EDGE,{"derivedFrom":sQuery(id+"F0.wireOp",EDGE,"E1.trimOffspring")}),1.0]])]}),makeQuery(id+"F2.imprint","IMPRINT",FACE,{"disambiguationData":[TD([[makeQuery(id+"F2.imprint","IMPRINT",EDGE,{"derivedFrom":sQuery(id+"F2.wireOp",EDGE,"E22.1.0")}),-1.0]])]})])]}),"instanceName":"9"});
            var Q22;
            Q22=makeQuery(id+"F7.opPattern","COPY",BODY,{"derivedFrom":makeQuery(id+"F3.opLoft","SWEPT_BODY",BODY,{"disambiguationData":[OSD([makeQuery(id+"F0.imprint","IMPRINT",FACE,{"disambiguationData":[TD([[makeQuery(id+"F0.imprint","IMPRINT",EDGE,{"derivedFrom":sQuery(id+"F0.wireOp",EDGE,"E1.trimOffspring")}),1.0]])]}),makeQuery(id+"F2.imprint","IMPRINT",FACE,{"disambiguationData":[TD([[makeQuery(id+"F2.imprint","IMPRINT",EDGE,{"derivedFrom":sQuery(id+"F2.wireOp",EDGE,"E22.1.0")}),-1.0]])]})])]}),"instanceName":"8"});
            var Q23;
            Q23=makeQuery(id+"F7.opPattern","COPY",BODY,{"derivedFrom":makeQuery(id+"F3.opLoft","SWEPT_BODY",BODY,{"disambiguationData":[OSD([makeQuery(id+"F0.imprint","IMPRINT",FACE,{"disambiguationData":[TD([[makeQuery(id+"F0.imprint","IMPRINT",EDGE,{"derivedFrom":sQuery(id+"F0.wireOp",EDGE,"E1.trimOffspring")}),1.0]])]}),makeQuery(id+"F2.imprint","IMPRINT",FACE,{"disambiguationData":[TD([[makeQuery(id+"F2.imprint","IMPRINT",EDGE,{"derivedFrom":sQuery(id+"F2.wireOp",EDGE,"E22.1.0")}),-1.0]])]})])]}),"instanceName":"6"});
            var Q24;
            Q24=makeQuery(id+"F7.opPattern","COPY",BODY,{"derivedFrom":makeQuery(id+"F3.opLoft","SWEPT_BODY",BODY,{"disambiguationData":[OSD([makeQuery(id+"F0.imprint","IMPRINT",FACE,{"disambiguationData":[TD([[makeQuery(id+"F0.imprint","IMPRINT",EDGE,{"derivedFrom":sQuery(id+"F0.wireOp",EDGE,"E1.trimOffspring")}),1.0]])]}),makeQuery(id+"F2.imprint","IMPRINT",FACE,{"disambiguationData":[TD([[makeQuery(id+"F2.imprint","IMPRINT",EDGE,{"derivedFrom":sQuery(id+"F2.wireOp",EDGE,"E22.1.0")}),-1.0]])]})])]}),"instanceName":"5"});
            var Q25;
            Q25=makeQuery(id+"F7.opPattern","COPY",BODY,{"derivedFrom":makeQuery(id+"F3.opLoft","SWEPT_BODY",BODY,{"disambiguationData":[OSD([makeQuery(id+"F0.imprint","IMPRINT",FACE,{"disambiguationData":[TD([[makeQuery(id+"F0.imprint","IMPRINT",EDGE,{"derivedFrom":sQuery(id+"F0.wireOp",EDGE,"E1.trimOffspring")}),1.0]])]}),makeQuery(id+"F2.imprint","IMPRINT",FACE,{"disambiguationData":[TD([[makeQuery(id+"F2.imprint","IMPRINT",EDGE,{"derivedFrom":sQuery(id+"F2.wireOp",EDGE,"E22.1.0")}),-1.0]])]})])]}),"instanceName":"7"});
            var Q26;
            Q26=makeQuery(id+"F7.opPattern","COPY",BODY,{"derivedFrom":makeQuery(id+"F3.opLoft","SWEPT_BODY",BODY,{"disambiguationData":[OSD([makeQuery(id+"F0.imprint","IMPRINT",FACE,{"disambiguationData":[TD([[makeQuery(id+"F0.imprint","IMPRINT",EDGE,{"derivedFrom":sQuery(id+"F0.wireOp",EDGE,"E1.trimOffspring")}),1.0]])]}),makeQuery(id+"F2.imprint","IMPRINT",FACE,{"disambiguationData":[TD([[makeQuery(id+"F2.imprint","IMPRINT",EDGE,{"derivedFrom":sQuery(id+"F2.wireOp",EDGE,"E22.1.0")}),-1.0]])]})])]}),"instanceName":"3"});
            var Q27;
            Q27=makeQuery(id+"F7.opPattern","COPY",BODY,{"derivedFrom":makeQuery(id+"F3.opLoft","SWEPT_BODY",BODY,{"disambiguationData":[OSD([makeQuery(id+"F0.imprint","IMPRINT",FACE,{"disambiguationData":[TD([[makeQuery(id+"F0.imprint","IMPRINT",EDGE,{"derivedFrom":sQuery(id+"F0.wireOp",EDGE,"E1.trimOffspring")}),1.0]])]}),makeQuery(id+"F2.imprint","IMPRINT",FACE,{"disambiguationData":[TD([[makeQuery(id+"F2.imprint","IMPRINT",EDGE,{"derivedFrom":sQuery(id+"F2.wireOp",EDGE,"E22.1.0")}),-1.0]])]})])]}),"instanceName":"2"});
            var Q28;
            Q28=makeQuery(id+"F7.opPattern","COPY",BODY,{"derivedFrom":makeQuery(id+"F3.opLoft","SWEPT_BODY",BODY,{"disambiguationData":[OSD([makeQuery(id+"F0.imprint","IMPRINT",FACE,{"disambiguationData":[TD([[makeQuery(id+"F0.imprint","IMPRINT",EDGE,{"derivedFrom":sQuery(id+"F0.wireOp",EDGE,"E1.trimOffspring")}),1.0]])]}),makeQuery(id+"F2.imprint","IMPRINT",FACE,{"disambiguationData":[TD([[makeQuery(id+"F2.imprint","IMPRINT",EDGE,{"derivedFrom":sQuery(id+"F2.wireOp",EDGE,"E22.1.0")}),-1.0]])]})])]}),"instanceName":"17"});
            var Q29;
            Q29=makeQuery(id+"F7.opPattern","COPY",BODY,{"derivedFrom":makeQuery(id+"F3.opLoft","SWEPT_BODY",BODY,{"disambiguationData":[OSD([makeQuery(id+"F0.imprint","IMPRINT",FACE,{"disambiguationData":[TD([[makeQuery(id+"F0.imprint","IMPRINT",EDGE,{"derivedFrom":sQuery(id+"F0.wireOp",EDGE,"E1.trimOffspring")}),1.0]])]}),makeQuery(id+"F2.imprint","IMPRINT",FACE,{"disambiguationData":[TD([[makeQuery(id+"F2.imprint","IMPRINT",EDGE,{"derivedFrom":sQuery(id+"F2.wireOp",EDGE,"E22.1.0")}),-1.0]])]})])]}),"instanceName":"20"});
            booleanBodies(context, id + "F8", {"operationType" : BooleanOperationType.UNION, "tools" : qUnion([Q0, Q1, Q2, Q3, Q4, Q5, Q6, Q7, Q8, Q9, Q10, Q11, Q12, Q13, Q14, Q15, Q16, Q17, Q18, Q19, Q20, Q21, Q22, Q23, Q24, Q25, Q26, Q27, Q28, Q29])});
        }
        {
            var Q0;
            {var subQ3=makeQuery(id+"F6.boolean.opBoolean","MERGE",FACE,{"derivedFrom":[makeQuery(id+"F3.opLoft","CAP_FACE",FACE,{"disambiguationData":[OSD([makeQuery(id+"F2.imprint","IMPRINT",FACE,{"disambiguationData":[TD([[makeQuery(id+"F2.imprint","IMPRINT",EDGE,{"derivedFrom":sQuery(id+"F2.wireOp",EDGE,"E22.1.0")}),-1.0]])]})])],"isStart":true}),makeQuery(id+"F6.opLoft","CAP_FACE",FACE,{"disambiguationData":[OSD([makeQuery(id+"F5.imprint","IMPRINT",FACE,{"disambiguationData":[TD([[makeQuery(id+"F5.imprint","IMPRINT",EDGE,{"derivedFrom":sQuery(id+"F5.wireOp",EDGE,"E24")}),1.0]])]})])],"isStart":true})]});Q0=makeQuery(id+"F8.opBoolean","MERGE",FACE,{"derivedFrom":[subQ3,makeQuery(id+"F7.opPattern","COPY",FACE,{"derivedFrom":subQ3,"instanceName":"1"}),makeQuery(id+"F7.opPattern","COPY",FACE,{"derivedFrom":subQ3,"instanceName":"2"}),makeQuery(id+"F7.opPattern","COPY",FACE,{"derivedFrom":subQ3,"instanceName":"3"}),makeQuery(id+"F7.opPattern","COPY",FACE,{"derivedFrom":subQ3,"instanceName":"4"}),makeQuery(id+"F7.opPattern","COPY",FACE,{"derivedFrom":subQ3,"instanceName":"5"}),makeQuery(id+"F7.opPattern","COPY",FACE,{"derivedFrom":subQ3,"instanceName":"6"}),makeQuery(id+"F7.opPattern","COPY",FACE,{"derivedFrom":subQ3,"instanceName":"7"}),makeQuery(id+"F7.opPattern","COPY",FACE,{"derivedFrom":subQ3,"instanceName":"8"}),makeQuery(id+"F7.opPattern","COPY",FACE,{"derivedFrom":subQ3,"instanceName":"9"}),makeQuery(id+"F7.opPattern","COPY",FACE,{"derivedFrom":subQ3,"instanceName":"10"}),makeQuery(id+"F7.opPattern","COPY",FACE,{"derivedFrom":subQ3,"instanceName":"11"}),makeQuery(id+"F7.opPattern","COPY",FACE,{"derivedFrom":subQ3,"instanceName":"12"}),makeQuery(id+"F7.opPattern","COPY",FACE,{"derivedFrom":subQ3,"instanceName":"13"}),makeQuery(id+"F7.opPattern","COPY",FACE,{"derivedFrom":subQ3,"instanceName":"14"}),makeQuery(id+"F7.opPattern","COPY",FACE,{"derivedFrom":subQ3,"instanceName":"15"}),makeQuery(id+"F7.opPattern","COPY",FACE,{"derivedFrom":subQ3,"instanceName":"16"}),makeQuery(id+"F7.opPattern","COPY",FACE,{"derivedFrom":subQ3,"instanceName":"17"}),makeQuery(id+"F7.opPattern","COPY",FACE,{"derivedFrom":subQ3,"instanceName":"18"}),makeQuery(id+"F7.opPattern","COPY",FACE,{"derivedFrom":subQ3,"instanceName":"19"}),makeQuery(id+"F7.opPattern","COPY",FACE,{"derivedFrom":subQ3,"instanceName":"20"}),makeQuery(id+"F7.opPattern","COPY",FACE,{"derivedFrom":subQ3,"instanceName":"21"}),makeQuery(id+"F7.opPattern","COPY",FACE,{"derivedFrom":subQ3,"instanceName":"22"}),makeQuery(id+"F7.opPattern","COPY",FACE,{"derivedFrom":subQ3,"instanceName":"23"}),makeQuery(id+"F7.opPattern","COPY",FACE,{"derivedFrom":subQ3,"instanceName":"24"}),makeQuery(id+"F7.opPattern","COPY",FACE,{"derivedFrom":subQ3,"instanceName":"25"}),makeQuery(id+"F7.opPattern","COPY",FACE,{"derivedFrom":subQ3,"instanceName":"26"}),makeQuery(id+"F7.opPattern","COPY",FACE,{"derivedFrom":subQ3,"instanceName":"27"}),makeQuery(id+"F7.opPattern","COPY",FACE,{"derivedFrom":subQ3,"instanceName":"28"}),makeQuery(id+"F7.opPattern","COPY",FACE,{"derivedFrom":subQ3,"instanceName":"29"})]});}
            var sketch = newSketch(context, id + "F9", { "sketchPlane" : qUnion([Q0])});
            skCircle(sketch, "E25", {"center": v(0, 0) * mm, "radius": 6.35 * mm});
            skSolve(sketch);
        }
        {
            var Q0;
            Q0 = qSketchRegion(id + "F9", true);
            extrude(context, id + "F10", {"entities" : qUnion([Q0]), "operationType" : NewBodyOperationType.REMOVE, "endBound" : BoundingType.THROUGH_ALL, "oppositeDirection" : true, "depth" : 25.4 * mm});
        }
    });
